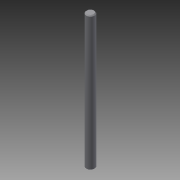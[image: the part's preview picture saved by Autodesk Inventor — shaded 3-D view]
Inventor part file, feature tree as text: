
AUTODESK INVENTOR PART (.ipt)
format: ipt  version: 2015 (Build 190159000, 159)  size: 82,432 bytes
history: native  units: in
note: dims shown in document units (in); Inventor stores cm internally (conversion verified against a paired STEP export)
features: other x3, extrude x1, chamfer x1, sketch x1
ambient origin geometry x8: Origin, YZ Plane, XZ Plane, XY Plane, X Axis, Y Axis, Z Axis, Center Point
bodies: Solid1 (feature_tree)
feature tree (6):
  other  "Axle-100mm - 739088.ipt"
  extrude  "Extrusion1"  Depth=0.9843in TaperAngle=0.0deg
  chamfer  "Chamfer1"  Distance=0.0197in Angle=45.0deg
  other  "tetrix_739088_2013::Axle-100mm - 739088.ipt"
  other  "TaggingFeature1"
  sketch  "Sketch1"  dims[d0=0.3937in d1=0.9843in d2=0.0in d3=0.0197in d4=0.125in d5=45.0deg]
